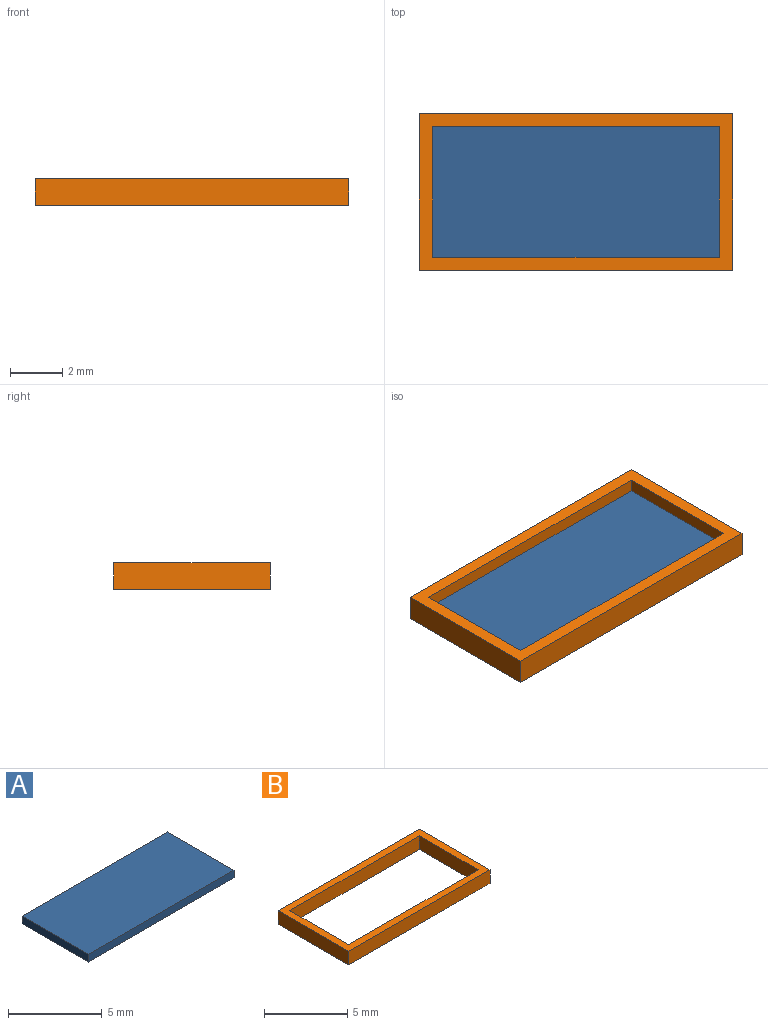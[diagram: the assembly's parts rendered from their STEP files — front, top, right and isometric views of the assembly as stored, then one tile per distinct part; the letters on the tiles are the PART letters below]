
ASSEMBLY  parts=2 mates=1
PART A: 6 faces, bbox 11x5x0.5 mm
  f0: plane 5x0.5mm, normal (1,0,0), area 2.5mm2, adj f1,f3,f4,f5
  f1: plane 11x0.5mm, normal (0,1,0), area 5.5mm2, adj f0,f2,f4,f5
  f2: plane 5x0.5mm, normal (-1,0,0), area 2.5mm2, adj f1,f3,f4,f5
  f3: plane 11x0.5mm, normal (0,-1,0), area 5.5mm2, adj f0,f2,f4,f5
  f4: plane 11x5mm, normal (0,0,1), area 55mm2, adj f0,f1,f2,f3
  f5: plane 11x5mm, normal (0,0,-1), area 55mm2, adj f0,f1,f2,f3
PART B: 10 faces, bbox 12x6x1 mm
  f0: plane 11x1mm, normal (0,-1,0), area 11mm2, adj f1,f7,f8,f9
  f1: plane 5x1mm, normal (-1,0,0), area 5mm2, adj f0,f2,f8,f9
  f2: plane 11x1mm, normal (0,1,0), area 11mm2, adj f1,f7,f8,f9
  f3: plane 6x1mm, normal (1,0,0), area 6mm2, adj f4,f6,f8,f9
  f4: plane 12x1mm, normal (0,1,0), area 12mm2, adj f3,f5,f8,f9
  f5: plane 6x1mm, normal (-1,0,0), area 6mm2, adj f4,f6,f8,f9
  f6: plane 12x1mm, normal (0,-1,0), area 12mm2, adj f3,f5,f8,f9
  f7: plane 5x1mm, normal (1,0,0), area 5mm2, adj f0,f2,f8,f9
  f8: plane 12x6mm, normal (0,0,1), area 17mm2, adj f0,f1,f2,f3,f4,f5,f6,f7
  f9: plane 12x6mm, normal (0,0,-1), area 17mm2, adj f0,f1,f2,f3,f4,f5,f6,f7
PLACE A t=(-0.09,0.03,-0.38)mm
PLACE B t=(-0.09,0.03,-0.38)mm
MATE fastened B.f9 <-> A.f5  axis (0,0,-1) through (-0.09,0.03,-0.38)mm
